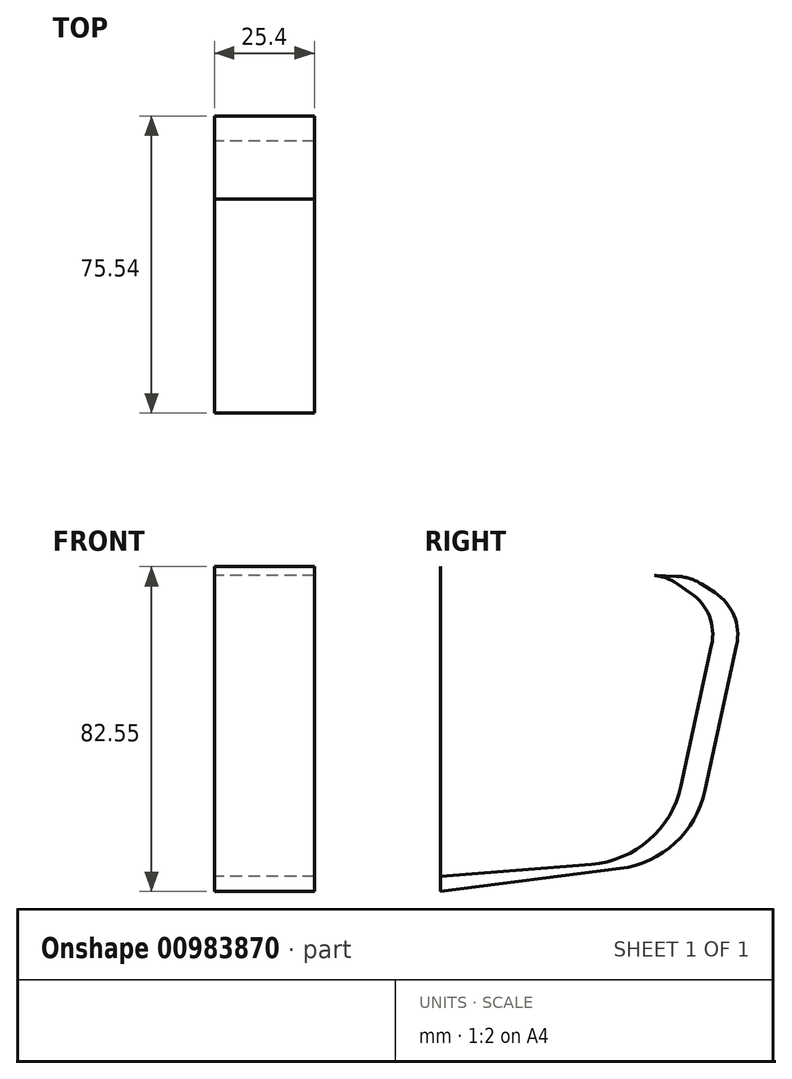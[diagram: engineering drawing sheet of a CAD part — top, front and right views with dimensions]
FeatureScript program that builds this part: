
annotation { "Feature Type Name" : "Feature", "Feature Type Description" : "" }
export const myFeature = defineFeature(function(context is Context, id is Id, definition is map)
    precondition{}
    {
        {
            var Q0;
            Q0=qCreatedBy(makeId("Right.planeOp"),FACE);
            var sketch = newSketch(context, id + "F0", { "sketchPlane" : qUnion([Q0])});
            skLineSegment(sketch, "E0", {"start": v(0, 96.3) * mm, "end": v(59.99, 93.88) * mm});
            skLineSegment(sketch, "E1", {"start": v(66.36, 91.87) * mm, "end": v(69.72, 89.7) * mm});
            skLineSegment(sketch, "E2", {"start": v(75.25, 76.33) * mm, "end": v(67.25, 39.43) * mm});
            skLineSegment(sketch, "E3", {"start": v(45.66, 19.62) * mm, "end": v(0, 13.75) * mm});
            skLineSegment(sketch, "E4", {"start": v(0, 96.3) * mm, "end": v(0, 13.75) * mm});
            skPoint(sketch, "E5.visualSharp", {"position": v(63.45, 93.74) * mm});
            skArc(sketch, "E5.filletArc", {"start": v(66.36, 91.87) * mm, "mid": v(63.3, 93.3) * mm, "end": v(59.99, 93.88) * mm});
            skPoint(sketch, "E6.visualSharp", {"position": v(77.11, 84.93) * mm});
            skArc(sketch, "E6.filletArc", {"start": v(75.25, 76.33) * mm, "mid": v(74.57, 83.88) * mm, "end": v(69.72, 89.7) * mm});
            skPoint(sketch, "E7.visualSharp", {"position": v(63.45, 21.9) * mm});
            skArc(sketch, "E7.filletArc", {"start": v(45.66, 19.62) * mm, "mid": v(59.6, 26.1) * mm, "end": v(67.25, 39.43) * mm});
            skSolve(sketch);
        }
        {
            var Q0;
            Q0=makeQuery(id+"F0.imprint","IMPRINT",FACE,{"disambiguationData":[TD([[makeQuery(id+"F0.imprint","IMPRINT",EDGE,{"derivedFrom":sQuery(id+"F0.wireOp",EDGE,"E0")}),-1.0]])]});
            extrude(context, id + "F1", {"entities" : qUnion([Q0]), "depth" : 25.4 * mm, "offsetDistance" : 25.4 * mm});
        }
        {
            var Q0;
            Q0=qCreatedBy(makeId("Right.planeOp"),FACE);
            var sketch = newSketch(context, id + "F2", { "sketchPlane" : qUnion([Q0])});
            skLineSegment(sketch, "E8", {"start": v(0.05, 96.34) * mm, "end": v(53.5, 94.18) * mm});
            skLineSegment(sketch, "E9", {"start": v(60.17, 91.96) * mm, "end": v(63.68, 89.55) * mm});
            skLineSegment(sketch, "E10", {"start": v(68.9, 76.4) * mm, "end": v(61.14, 40.61) * mm});
            skLineSegment(sketch, "E11", {"start": v(38.36, 20.68) * mm, "end": v(0.05, 17.6) * mm});
            skLineSegment(sketch, "E12", {"start": v(0.05, 96.34) * mm, "end": v(0.05, 17.6) * mm});
            skPoint(sketch, "E13.visualSharp", {"position": v(57.15, 94.03) * mm});
            skArc(sketch, "E13.filletArc", {"start": v(60.17, 91.96) * mm, "mid": v(56.99, 93.54) * mm, "end": v(53.5, 94.18) * mm});
            skPoint(sketch, "E14.visualSharp", {"position": v(70.7, 84.72) * mm});
            skArc(sketch, "E14.filletArc", {"start": v(68.9, 76.4) * mm, "mid": v(68.3, 83.77) * mm, "end": v(63.68, 89.55) * mm});
            skPoint(sketch, "E15.visualSharp", {"position": v(57.15, 22.19) * mm});
            skArc(sketch, "E15.filletArc", {"start": v(38.36, 20.68) * mm, "mid": v(53.05, 26.88) * mm, "end": v(61.14, 40.61) * mm});
            skSolve(sketch);
        }
        {
            var Q0;
            Q0=makeQuery(id+"F2.imprint","IMPRINT",FACE,{"disambiguationData":[TD([[makeQuery(id+"F2.imprint","IMPRINT",EDGE,{"derivedFrom":sQuery(id+"F2.wireOp",EDGE,"E8")}),-1.0]])]});
            extrude(context, id + "F3", {"entities" : qUnion([Q0]), "operationType" : NewBodyOperationType.REMOVE, "depth" : 25.4 * mm, "offsetDistance" : 25.4 * mm});
        }
    });
